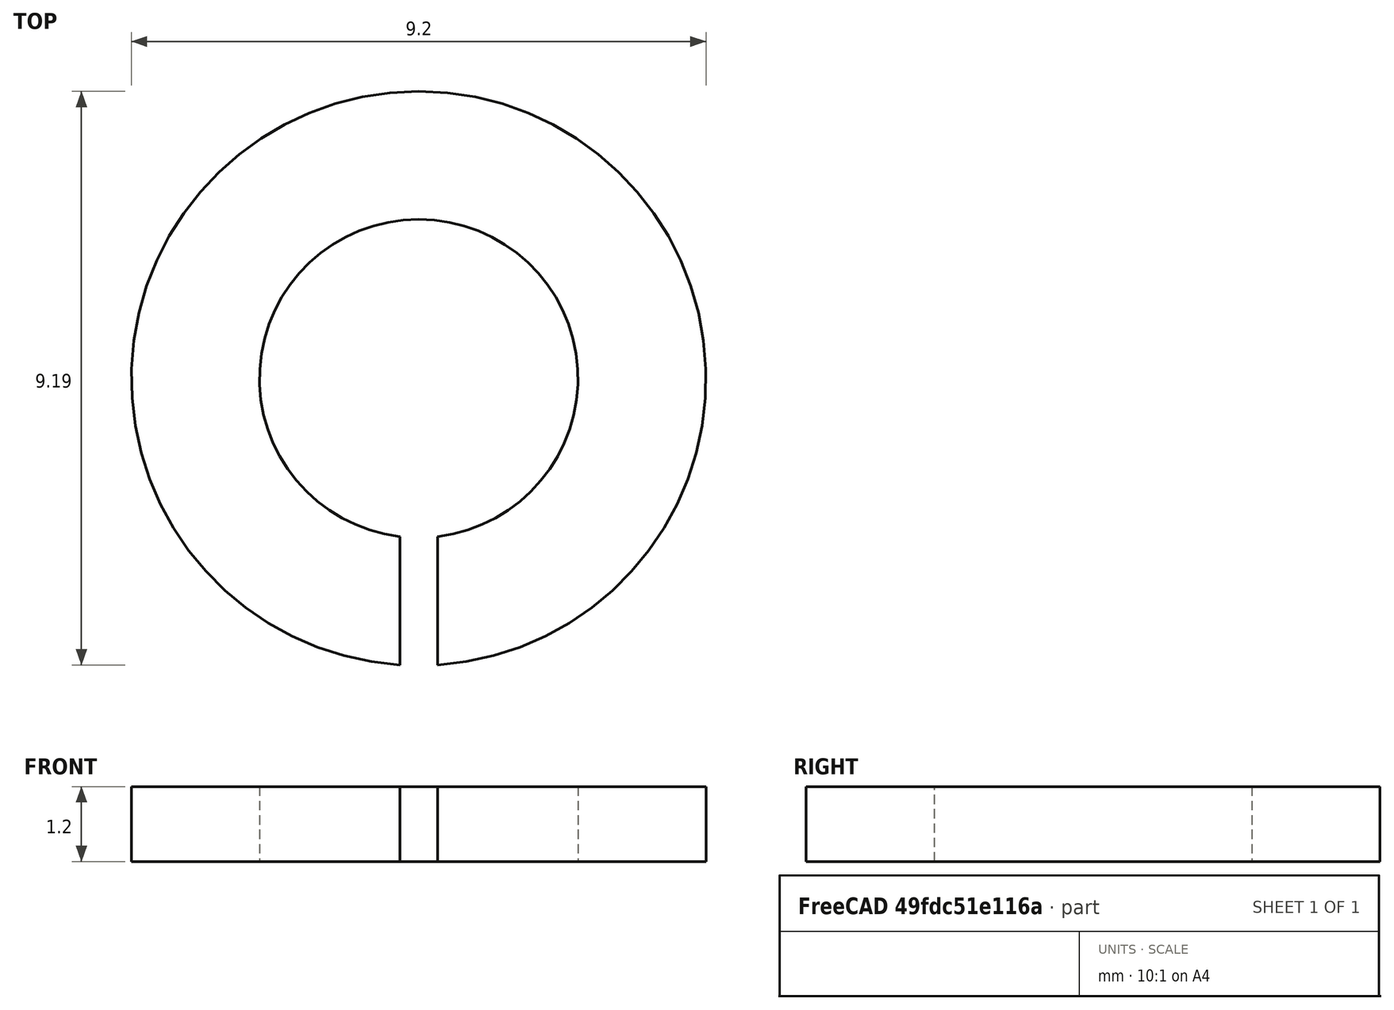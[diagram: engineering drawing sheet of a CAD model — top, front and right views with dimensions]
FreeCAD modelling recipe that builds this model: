
FCSTD DOCUMENT  (FreeCAD 0.15R4651 (Git))
Label: Federring_DIN127-B5
License: All rights reserved
LicenseURL: http://de.wikipedia.org/wiki/Alle_Rechte_vorbehalten
objects: Sketcher::SketchObject×1, PartDesign::Pad×1
note: 3 computed .brp shape members not serialized (recipe doc carries the construction recipe); baked Part::Feature solids carry a one-line shape summary decoded from their .brp

FEATURE [Sketcher::SketchObject] Sketch
  sketch-geometry (4):
    g0: ArcOfCircle CenterX=0 CenterY=0 CenterZ=0 NormalX=0 NormalY=0 NormalZ=1 Radius=2.55 StartAngle=4.83031 EndAngle=10.8777
    g1: ArcOfCircle CenterX=0 CenterY=0 CenterZ=0 NormalX=0 NormalY=0 NormalZ=1 Radius=4.6 StartAngle=4.77765 EndAngle=10.9303
    g2: LineSegment StartX=0.3 StartY=-2.53229 StartZ=0 EndX=0.3 EndY=-4.59021 EndZ=0
    g3: LineSegment StartX=-0.3 StartY=-4.59021 StartZ=0 EndX=-0.3 EndY=-2.53229 EndZ=0
  constraints (12):
    c: Coincident(g0,g-1)
    c: Coincident(g1,g-1)
    c: Vertical(g2)
    c: Vertical(g3)
    c: Coincident(g0,g2)
    c: Coincident(g0,g3)
    c: Coincident(g1,g2)
    c: Coincident(g1,g3)
    c: Symmetric(g1,g1,g-2)
    c: Radius(g0) = 2.55
    c: Radius(g1) = 4.6
    c: DistanceX(g1,g1) = -0.6
FEATURE [PartDesign::Pad] Pad  label="Federring DIN 127-B 5 #"
  Length = 1.2
  Length2 = 100
  Midplane = true
  Sketch = -> Sketch
  Type = 0
